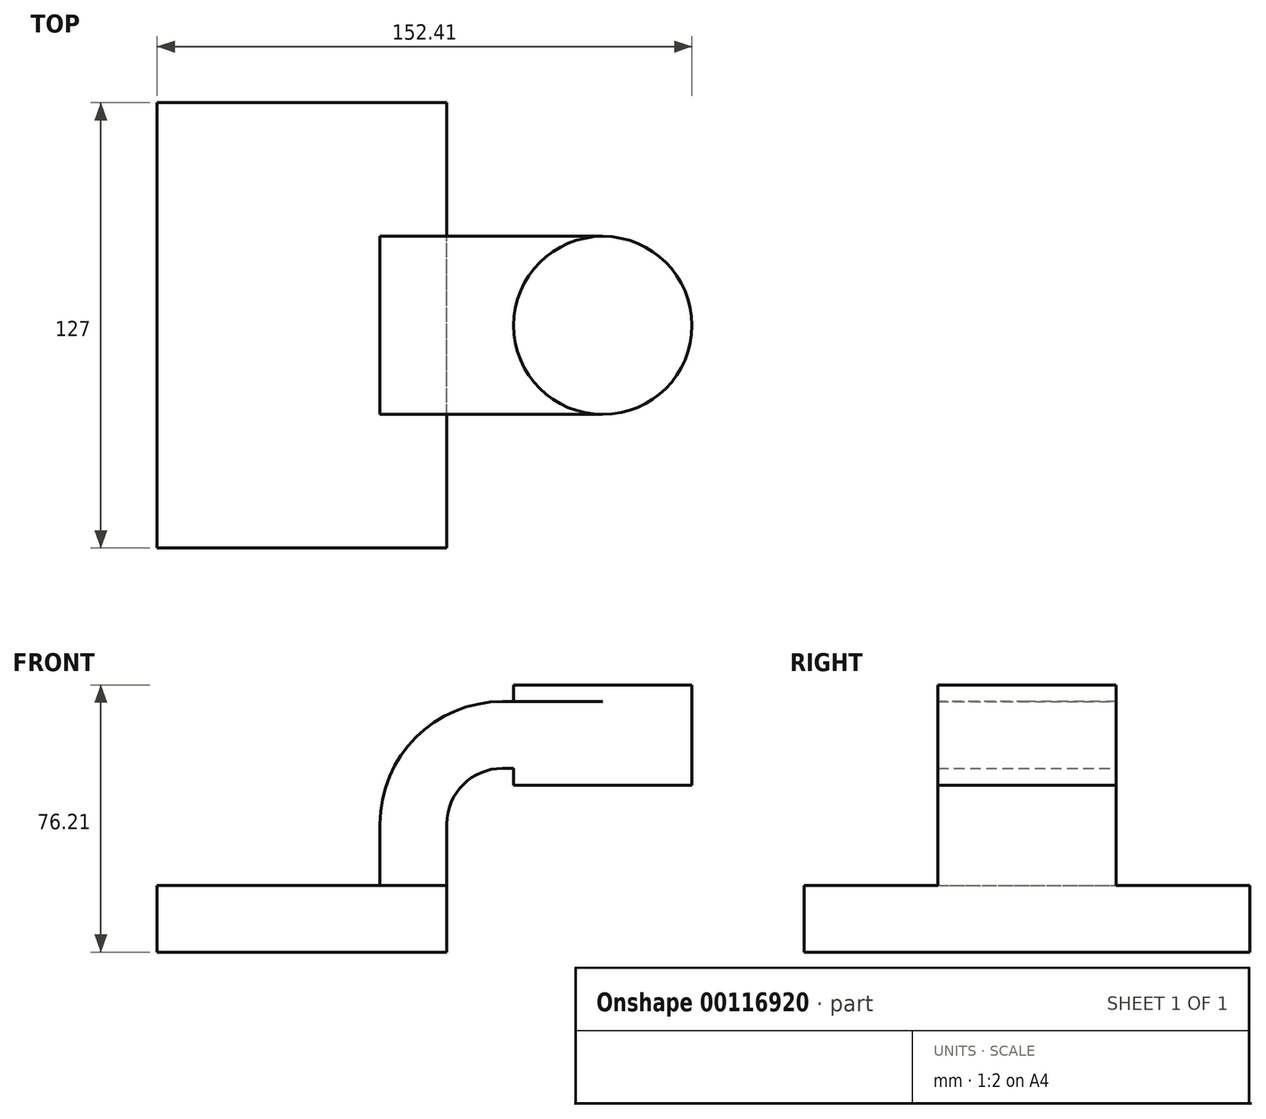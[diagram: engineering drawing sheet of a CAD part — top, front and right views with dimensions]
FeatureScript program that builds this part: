
annotation { "Feature Type Name" : "Feature", "Feature Type Description" : "" }
export const myFeature = defineFeature(function(context is Context, id is Id, definition is map)
    precondition{}
    {
        {
            var Q0;
            Q0=qCreatedBy(makeId("Front.planeOp"),FACE);
            var sketch = newSketch(context, id + "F0", { "sketchPlane" : qUnion([Q0])});
            skLineSegment(sketch, "E0.bottom", {"start": v(-41.28, -9.53) * mm, "end": v(41.28, -9.53) * mm});
            skLineSegment(sketch, "E0.top", {"start": v(-41.28, 9.53) * mm, "end": v(41.28, 9.53) * mm});
            skLineSegment(sketch, "E0.left", {"start": v(-41.28, -9.53) * mm, "end": v(-41.28, 9.53) * mm});
            skLineSegment(sketch, "E0.right", {"start": v(41.28, -9.53) * mm, "end": v(41.28, 9.53) * mm});
            skPoint(sketch, "E0.middle", {"position": v(0, 0) * mm});
            skLineSegment(sketch, "E1.bottom", {"start": v(60.32, 38.1) * mm, "end": v(111.12, 38.1) * mm});
            skLineSegment(sketch, "E1.top", {"start": v(60.32, 66.67) * mm, "end": v(111.12, 66.67) * mm});
            skLineSegment(sketch, "E1.left", {"start": v(60.32, 38.1) * mm, "end": v(60.32, 66.67) * mm});
            skLineSegment(sketch, "E1.right", {"start": v(111.12, 38.1) * mm, "end": v(111.12, 66.67) * mm});
            skPoint(sketch, "E1.middle", {"position": v(85.72, 52.39) * mm});
            skLineSegment(sketch, "E2", {"start": v(41.28, 9.53) * mm, "end": v(41.28, 27) * mm});
            skArc(sketch, "E3", {"start": v(41.27, 27) * mm, "mid": v(45.92, 38.23) * mm, "end": v(57.15, 42.88) * mm});
            skLineSegment(sketch, "E4", {"start": v(57.15, 42.88) * mm, "end": v(85.65, 42.88) * mm});
            skLineSegment(sketch, "E5.0", {"start": v(57.15, 61.93) * mm, "end": v(85.72, 61.93) * mm});
            skArc(sketch, "E5.1", {"start": v(22.23, 27) * mm, "mid": v(32.45, 51.7) * mm, "end": v(57.15, 61.93) * mm});
            skLineSegment(sketch, "E5.2", {"start": v(22.22, 9.53) * mm, "end": v(22.22, 27) * mm});
            skLineSegment(sketch, "E6", {"start": v(85.73, 38.1) * mm, "end": v(85.73, 66.67) * mm});
            skFitSpline(sketch, "E7", {"points": [v(-41.28, 9.53) * mm, v(57.15, 61.93) * mm], "startDerivative": vector(123.83, 38.17) * mm, "endDerivative": vector(41.45, -23.6) * mm});
            skSolve(sketch);
        }
        {
            var Q0;
            Q0=makeQuery(id+"F0.imprint","IMPRINT",FACE,{"disambiguationData":[TD([[makeQuery(id+"F0.imprint","IMPRINT",EDGE,{"derivedFrom":sQuery(id+"F0.wireOp",EDGE,"E0.bottom")}),1.0]])]});
            extrude(context, id + "F1", {"entities" : qUnion([Q0]), "endBound" : BoundingType.SYMMETRIC, "depth" : 127 * mm});
        }
        {
            var Q0;
            {var subQ2=sQuery(id+"F0.wireOp",EDGE,"E2");Q0=makeQuery(id+"F0.imprint","IMPRINT",FACE,{"disambiguationData":[TD([[makeQuery(id+"F0.imprint","IMPRINT",EDGE,{"derivedFrom":subQ2}),1.0]])]});}
            var Q1;
            {var subQ3=sQuery(id+"F0.wireOp",EDGE,"E1.left");var subQ6=sQuery(id+"F0.wireOp",EDGE,"E1.bottom");var subQ7=makeQuery(id+"F0.imprint","INTERSECT",VERTEX,{"derivedFrom":[subQ6,subQ3]});Q1=makeQuery(id+"F0.imprint","IMPRINT",FACE,{"disambiguationData":[TD([[makeQuery(id+"F0.imprint","IMPRINT",EDGE,{"disambiguationData":[TD([[subQ7,-1.0]])],"derivedFrom":subQ6}),1.0]])]});}
            extrude(context, id + "F2", {"entities" : qUnion([Q0, Q1]), "operationType" : NewBodyOperationType.ADD, "endBound" : BoundingType.SYMMETRIC, "depth" : 50.8 * mm});
        }
        {
            var Q0;
            Q0=makeQuery(id+"F0.imprint","IMPRINT",FACE,{"disambiguationData":[TD([[makeQuery(id+"F0.imprint","IMPRINT",EDGE,{"derivedFrom":sQuery(id+"F0.wireOp",EDGE,"E5.1")}),1.0]])]});
            extrude(context, id + "F3", {"entities" : qUnion([Q0]), "operationType" : NewBodyOperationType.ADD, "endBound" : BoundingType.SYMMETRIC, "depth" : 15.88 * mm});
        }
        {
            var Q0;
            {var subQ0=sQuery(id+"F0.wireOp",EDGE,"E1.right");Q0=makeQuery(id+"F0.imprint","IMPRINT",FACE,{"disambiguationData":[TD([[makeQuery(id+"F0.imprint","IMPRINT",EDGE,{"derivedFrom":subQ0}),1.0]])]});}
            var Q1;
            Q1=sQuery(id+"F0.wireOp",EDGE,"E6");
            revolve(context, id + "F4", {"operationType" : NewBodyOperationType.ADD, "entities" : qUnion([Q0]), "axis" : qUnion([Q1]), "revolveType" : RevolveType.FULL});
        }
    });
